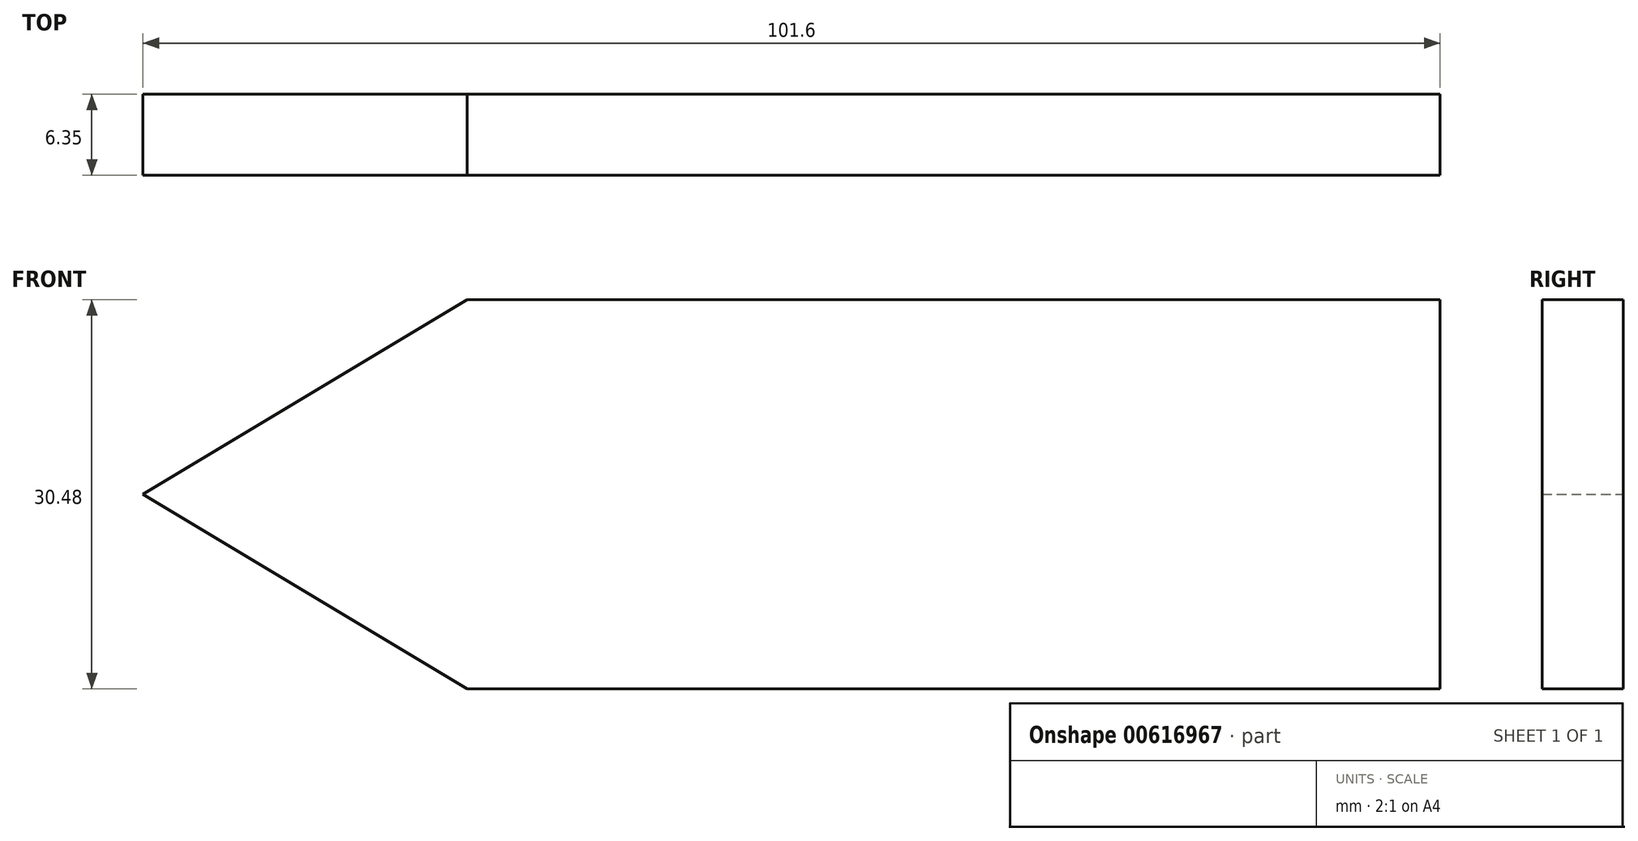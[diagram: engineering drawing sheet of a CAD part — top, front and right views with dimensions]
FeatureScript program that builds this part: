
annotation { "Feature Type Name" : "Feature", "Feature Type Description" : "" }
export const myFeature = defineFeature(function(context is Context, id is Id, definition is map)
    precondition{}
    {
        {
            var Q0;
            Q0=qCreatedBy(makeId("Front.planeOp"),FACE);
            var sketch = newSketch(context, id + "F0", { "sketchPlane" : qUnion([Q0])});
            skLineSegment(sketch, "E0", {"start": v(-62.37, 35.4) * mm, "end": v(13.83, 35.4) * mm});
            skLineSegment(sketch, "E1", {"start": v(13.83, 35.4) * mm, "end": v(13.83, 4.93) * mm});
            skLineSegment(sketch, "E2", {"start": v(13.83, 4.93) * mm, "end": v(-62.37, 4.93) * mm});
            skLineSegment(sketch, "E3", {"start": v(-87.77, 20.17) * mm, "end": v(-62.37, 35.4) * mm});
            skLineSegment(sketch, "E4", {"start": v(-87.77, 20.17) * mm, "end": v(-62.37, 4.93) * mm});
            skSolve(sketch);
        }
        {
            var Q0;
            Q0 = qSketchRegion(id + "F0", true);
            extrude(context, id + "F1", {"entities" : qUnion([Q0]), "depth" : 6.35 * mm, "offsetDistance" : 25.4 * mm});
        }
    });
